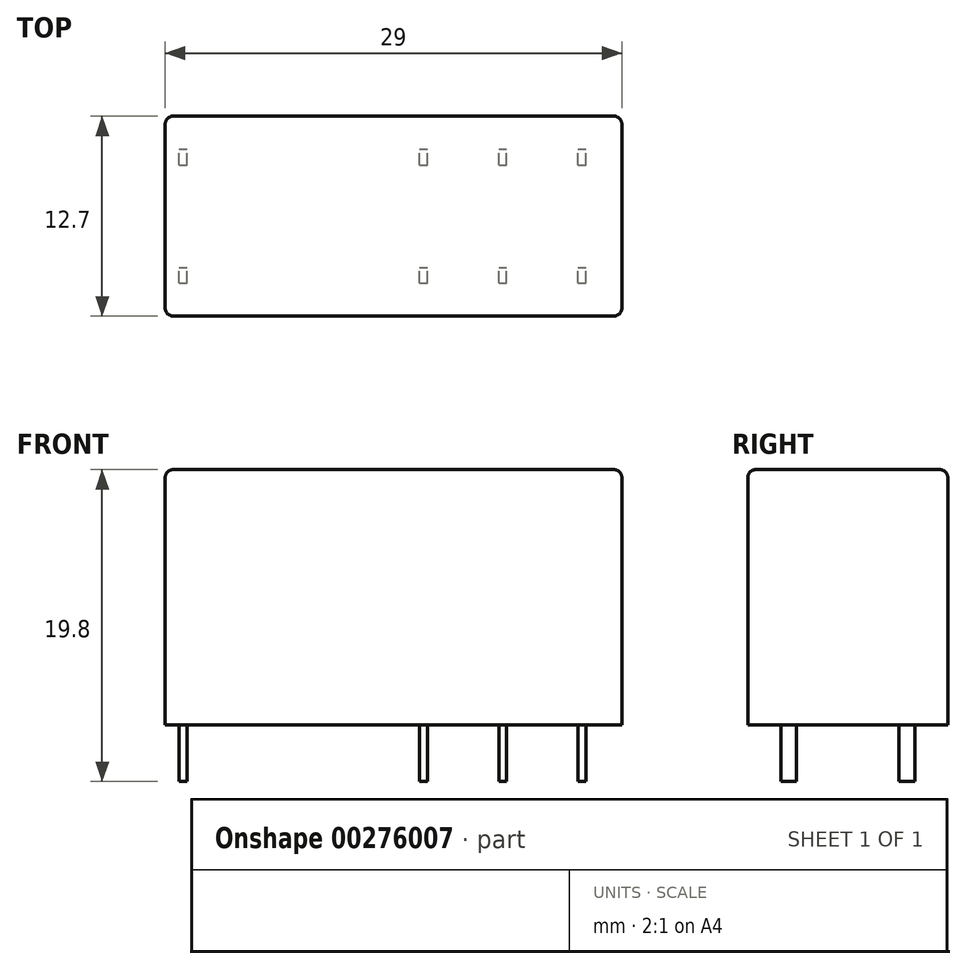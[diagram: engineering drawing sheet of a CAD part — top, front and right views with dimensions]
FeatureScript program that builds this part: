
annotation { "Feature Type Name" : "Feature", "Feature Type Description" : "" }
export const myFeature = defineFeature(function(context is Context, id is Id, definition is map)
    precondition{}
    {
        {
            var Q0;
            Q0=qCreatedBy(makeId("Front.planeOp"),FACE);
            var sketch = newSketch(context, id + "F0", { "sketchPlane" : qUnion([Q0])});
            skLineSegment(sketch, "E0.bottom", {"start": v(-14.5, 8.1) * mm, "end": v(14.5, 8.1) * mm});
            skLineSegment(sketch, "E0.top", {"start": v(-14.5, -8.1) * mm, "end": v(14.5, -8.1) * mm});
            skLineSegment(sketch, "E0.left", {"start": v(-14.5, 8.1) * mm, "end": v(-14.5, -8.1) * mm});
            skLineSegment(sketch, "E0.right", {"start": v(14.5, 8.1) * mm, "end": v(14.5, -8.1) * mm});
            skPoint(sketch, "E1", {"position": v(0, -8.1) * mm});
            skPoint(sketch, "E2", {"position": v(14.5, 0) * mm});
            skSolve(sketch);
        }
        {
            var Q0;
            Q0=makeQuery(id+"F0.imprint","IMPRINT",FACE,{"disambiguationData":[TD([[makeQuery(id+"F0.imprint","IMPRINT",EDGE,{"derivedFrom":sQuery(id+"F0.wireOp",EDGE,"E0.bottom")}),-1.0]])]});
            extrude(context, id + "F1", {"entities" : qUnion([Q0]), "depth" : 12.7 * mm});
        }
        {
            var Q0;
            Q0=makeQuery(id+"F1.opExtrude","SWEPT_FACE",FACE,{"disambiguationData":[OSD([sQuery(id+"F0.wireOp",EDGE,"E0.top")])]});
            var sketch = newSketch(context, id + "F2", { "sketchPlane" : qUnion([Q0])});
            skLineSegment(sketch, "E3.bottom", {"start": v(1.65, 10.6) * mm, "end": v(2.15, 10.6) * mm});
            skLineSegment(sketch, "E3.top", {"start": v(1.65, 9.6) * mm, "end": v(2.15, 9.6) * mm});
            skLineSegment(sketch, "E3.left", {"start": v(1.65, 10.6) * mm, "end": v(1.65, 9.6) * mm});
            skLineSegment(sketch, "E3.right", {"start": v(2.15, 10.6) * mm, "end": v(2.15, 9.6) * mm});
            skLineSegment(sketch, "E4.bottom", {"start": v(6.7, 10.6) * mm, "end": v(7.2, 10.6) * mm});
            skLineSegment(sketch, "E4.top", {"start": v(6.7, 9.6) * mm, "end": v(7.2, 9.6) * mm});
            skLineSegment(sketch, "E4.left", {"start": v(6.7, 10.6) * mm, "end": v(6.7, 9.6) * mm});
            skLineSegment(sketch, "E4.right", {"start": v(7.2, 10.6) * mm, "end": v(7.2, 9.6) * mm});
            skLineSegment(sketch, "E5.bottom", {"start": v(11.73, 10.6) * mm, "end": v(12.23, 10.6) * mm});
            skLineSegment(sketch, "E5.top", {"start": v(11.73, 9.6) * mm, "end": v(12.23, 9.6) * mm});
            skLineSegment(sketch, "E5.left", {"start": v(11.73, 10.6) * mm, "end": v(11.73, 9.6) * mm});
            skLineSegment(sketch, "E5.right", {"start": v(12.23, 10.6) * mm, "end": v(12.23, 9.6) * mm});
            skLineSegment(sketch, "E6.bottom", {"start": v(1.65, 3.1) * mm, "end": v(2.15, 3.1) * mm});
            skLineSegment(sketch, "E6.top", {"start": v(1.65, 2.1) * mm, "end": v(2.15, 2.1) * mm});
            skLineSegment(sketch, "E6.left", {"start": v(1.65, 3.1) * mm, "end": v(1.65, 2.1) * mm});
            skLineSegment(sketch, "E6.right", {"start": v(2.15, 3.1) * mm, "end": v(2.15, 2.1) * mm});
            skLineSegment(sketch, "E7.bottom", {"start": v(11.73, 3.1) * mm, "end": v(12.23, 3.1) * mm});
            skLineSegment(sketch, "E7.top", {"start": v(11.73, 2.1) * mm, "end": v(12.23, 2.1) * mm});
            skLineSegment(sketch, "E7.left", {"start": v(11.73, 3.1) * mm, "end": v(11.73, 2.1) * mm});
            skLineSegment(sketch, "E7.right", {"start": v(12.23, 3.1) * mm, "end": v(12.23, 2.1) * mm});
            skPoint(sketch, "E8", {"position": v(2.15, 2.6) * mm});
            skPoint(sketch, "E9", {"position": v(12.23, 2.6) * mm});
            skPoint(sketch, "E10", {"position": v(1.9, 3.1) * mm});
            skPoint(sketch, "E11", {"position": v(11.98, 3.1) * mm});
            skPoint(sketch, "E12", {"position": v(1.9, 10.6) * mm});
            skPoint(sketch, "E13", {"position": v(2.15, 10.1) * mm});
            skPoint(sketch, "E14", {"position": v(6.94, 10.6) * mm});
            skPoint(sketch, "E15", {"position": v(7.2, 10.1) * mm});
            skPoint(sketch, "E16", {"position": v(11.98, 10.6) * mm});
            skPoint(sketch, "E17", {"position": v(12.23, 10.1) * mm});
            skLineSegment(sketch, "E18.bottom", {"start": v(6.7, 3.1) * mm, "end": v(7.2, 3.1) * mm});
            skLineSegment(sketch, "E18.top", {"start": v(6.7, 2.1) * mm, "end": v(7.2, 2.1) * mm});
            skLineSegment(sketch, "E18.left", {"start": v(6.7, 3.1) * mm, "end": v(6.7, 2.1) * mm});
            skLineSegment(sketch, "E18.right", {"start": v(7.2, 3.1) * mm, "end": v(7.2, 2.1) * mm});
            skPoint(sketch, "E19", {"position": v(6.94, 3.1) * mm});
            skPoint(sketch, "E20", {"position": v(7.2, 2.6) * mm});
            skPoint(sketch, "E21", {"position": v(14.5, 6.35) * mm});
            skLineSegment(sketch, "E22.bottom", {"start": v(-13.61, 10.6) * mm, "end": v(-13.1, 10.6) * mm});
            skLineSegment(sketch, "E22.top", {"start": v(-13.61, 9.6) * mm, "end": v(-13.1, 9.6) * mm});
            skLineSegment(sketch, "E22.left", {"start": v(-13.61, 10.6) * mm, "end": v(-13.61, 9.6) * mm});
            skLineSegment(sketch, "E22.right", {"start": v(-13.11, 10.6) * mm, "end": v(-13.11, 9.6) * mm});
            skLineSegment(sketch, "E23.bottom", {"start": v(-13.61, 3.1) * mm, "end": v(-13.11, 3.1) * mm});
            skLineSegment(sketch, "E23.top", {"start": v(-13.61, 2.1) * mm, "end": v(-13.11, 2.1) * mm});
            skLineSegment(sketch, "E23.left", {"start": v(-13.61, 3.1) * mm, "end": v(-13.61, 2.1) * mm});
            skLineSegment(sketch, "E23.right", {"start": v(-13.11, 3.1) * mm, "end": v(-13.11, 2.1) * mm});
            skPoint(sketch, "E24", {"position": v(-13.36, 10.6) * mm});
            skPoint(sketch, "E25", {"position": v(-13.11, 10.1) * mm});
            skPoint(sketch, "E26", {"position": v(-13.36, 3.1) * mm});
            skPoint(sketch, "E27", {"position": v(-13.11, 2.6) * mm});
            skSolve(sketch);
        }
        {
            var Q0;
            Q0=makeQuery(id+"F2.imprint","IMPRINT",FACE,{"disambiguationData":[TD([[makeQuery(id+"F2.imprint","IMPRINT",EDGE,{"derivedFrom":sQuery(id+"F2.wireOp",EDGE,"vSG3JX7v-CeC8-yuF2-foI3-2tLnMHmi4EAO")}),1.0]])]});
            var Q1;
            Q1=makeQuery(id+"F2.imprint","IMPRINT",FACE,{"disambiguationData":[TD([[makeQuery(id+"F2.imprint","IMPRINT",EDGE,{"derivedFrom":sQuery(id+"F2.wireOp",EDGE,"4h4EXeac-sGDj-uKa5-xLSE-ufXuJjwVorfR")}),1.0]])]});
            var Q2;
            Q2=makeQuery(id+"F2.imprint","IMPRINT",FACE,{"disambiguationData":[TD([[makeQuery(id+"F2.imprint","IMPRINT",EDGE,{"derivedFrom":sQuery(id+"F2.wireOp",EDGE,"E6.bottom")}),-1.0]])]});
            var Q3;
            Q3=makeQuery(id+"F2.imprint","IMPRINT",FACE,{"disambiguationData":[TD([[makeQuery(id+"F2.imprint","IMPRINT",EDGE,{"derivedFrom":sQuery(id+"F2.wireOp",EDGE,"E3.bottom")}),-1.0]])]});
            var Q4;
            Q4=makeQuery(id+"F2.imprint","IMPRINT",FACE,{"disambiguationData":[TD([[makeQuery(id+"F2.imprint","IMPRINT",EDGE,{"derivedFrom":sQuery(id+"F2.wireOp",EDGE,"E4.bottom")}),-1.0]])]});
            var Q5;
            Q5=makeQuery(id+"F2.imprint","IMPRINT",FACE,{"disambiguationData":[TD([[makeQuery(id+"F2.imprint","IMPRINT",EDGE,{"derivedFrom":sQuery(id+"F2.wireOp",EDGE,"E5.bottom")}),-1.0]])]});
            var Q6;
            Q6=makeQuery(id+"F2.imprint","IMPRINT",FACE,{"disambiguationData":[TD([[makeQuery(id+"F2.imprint","IMPRINT",EDGE,{"derivedFrom":sQuery(id+"F2.wireOp",EDGE,"E18.bottom")}),-1.0]])]});
            var Q7;
            Q7=makeQuery(id+"F2.imprint","IMPRINT",FACE,{"disambiguationData":[TD([[makeQuery(id+"F2.imprint","IMPRINT",EDGE,{"derivedFrom":sQuery(id+"F2.wireOp",EDGE,"E7.bottom")}),-1.0]])]});
            var Q8;
            Q8=makeQuery(id+"F2.imprint","IMPRINT",FACE,{"disambiguationData":[TD([[makeQuery(id+"F2.imprint","IMPRINT",EDGE,{"derivedFrom":sQuery(id+"F2.wireOp",EDGE,"E22.bottom")}),-1.0]])]});
            var Q9;
            Q9=makeQuery(id+"F2.imprint","IMPRINT",FACE,{"disambiguationData":[TD([[makeQuery(id+"F2.imprint","IMPRINT",EDGE,{"derivedFrom":sQuery(id+"F2.wireOp",EDGE,"E23.bottom")}),-1.0]])]});
            extrude(context, id + "F3", {"entities" : qUnion([Q0, Q1, Q2, Q3, Q4, Q5, Q6, Q7, Q8, Q9]), "depth" : 3.6 * mm});
        }
        {
            var Q0;
            Q0=makeQuery(id+"F1.opExtrude","CAP_EDGE",EDGE,{"disambiguationData":[OSD([sQuery(id+"F0.wireOp",EDGE,"E0.left")])],"isStart":false});
            var Q1;
            Q1=makeQuery(id+"F1.opExtrude","CAP_EDGE",EDGE,{"disambiguationData":[OSD([sQuery(id+"F0.wireOp",EDGE,"E0.bottom")])],"isStart":false});
            var Q2;
            Q2=makeQuery(id+"F1.opExtrude","SWEPT_EDGE",EDGE,{"disambiguationData":[OSD([sQuery(id+"F0.wireOp",EDGE,"E0.bottom"),sQuery(id+"F0.wireOp",EDGE,"E0.left")])]});
            var Q3;
            Q3=makeQuery(id+"F1.opExtrude","CAP_EDGE",EDGE,{"disambiguationData":[OSD([sQuery(id+"F0.wireOp",EDGE,"E0.bottom")])],"isStart":true});
            var Q4;
            Q4=makeQuery(id+"F1.opExtrude","SWEPT_EDGE",EDGE,{"disambiguationData":[OSD([sQuery(id+"F0.wireOp",EDGE,"E0.bottom"),sQuery(id+"F0.wireOp",EDGE,"E0.right")])]});
            var Q5;
            Q5=makeQuery(id+"F1.opExtrude","CAP_EDGE",EDGE,{"disambiguationData":[OSD([sQuery(id+"F0.wireOp",EDGE,"E0.right")])],"isStart":false});
            var Q6;
            Q6=makeQuery(id+"F1.opExtrude","CAP_EDGE",EDGE,{"disambiguationData":[OSD([sQuery(id+"F0.wireOp",EDGE,"E0.right")])],"isStart":true});
            var Q7;
            Q7=makeQuery(id+"F1.opExtrude","CAP_EDGE",EDGE,{"disambiguationData":[OSD([sQuery(id+"F0.wireOp",EDGE,"E0.left")])],"isStart":true});
            fillet(context, id + "F4", {"entities" : qUnion([Q0, Q1, Q2, Q3, Q4, Q5, Q6, Q7]), "radius" : 0.5 * mm, "tangentPropagation" : true, "allowEdgeOverflow" : false});
        }
    });
